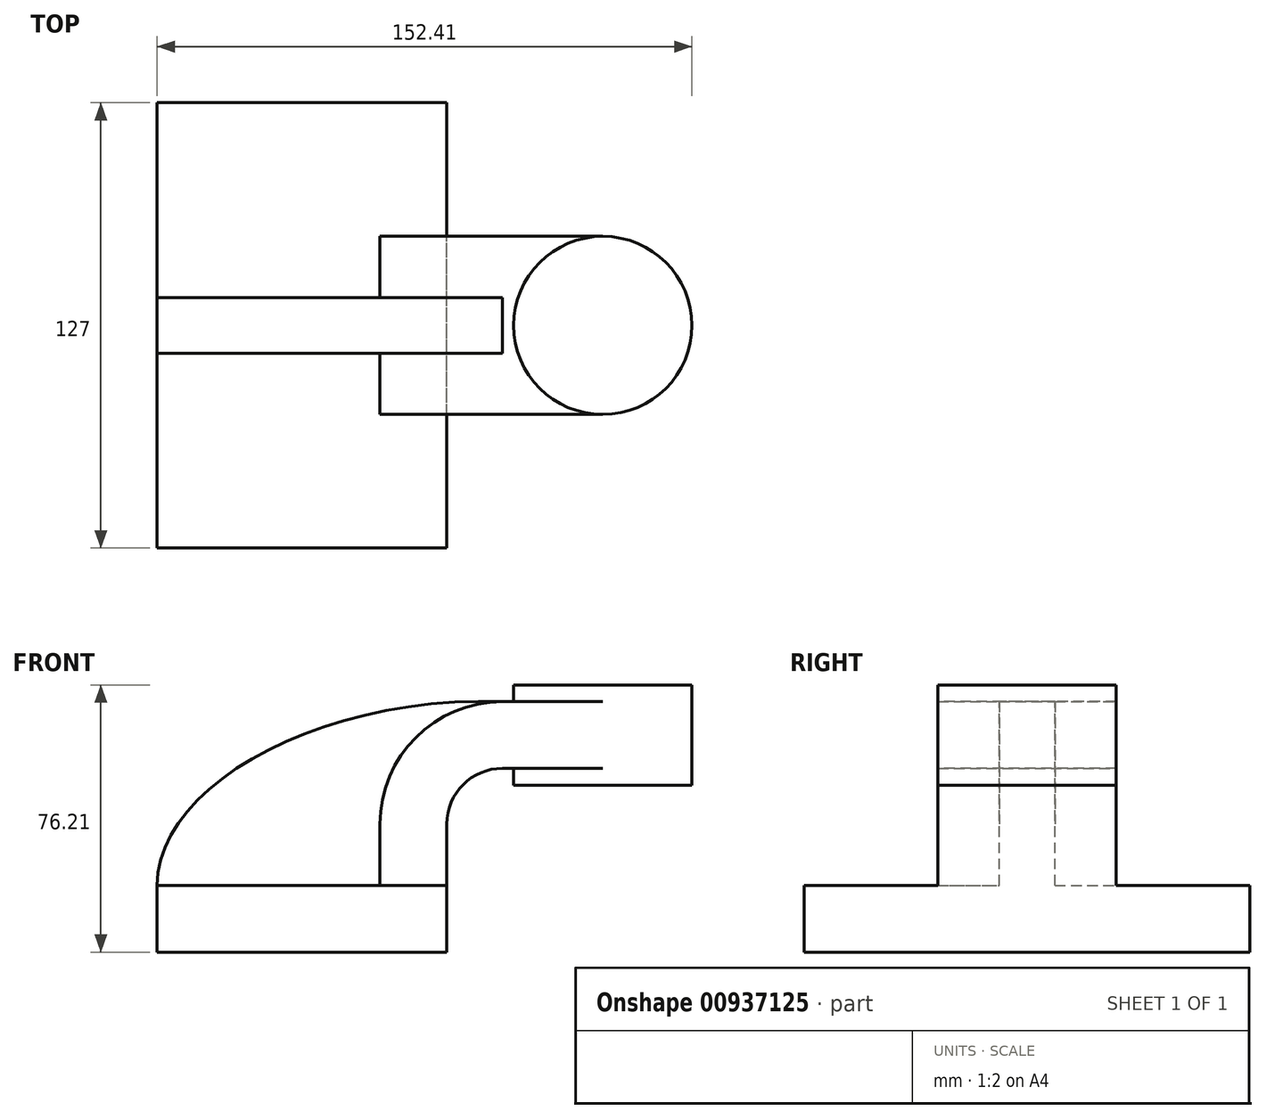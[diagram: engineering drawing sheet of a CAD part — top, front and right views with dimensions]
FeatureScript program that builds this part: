
annotation { "Feature Type Name" : "Feature", "Feature Type Description" : "" }
export const myFeature = defineFeature(function(context is Context, id is Id, definition is map)
    precondition{}
    {
        {
            var Q0;
            Q0=qCreatedBy(makeId("Front.planeOp"),FACE);
            var sketch = newSketch(context, id + "F0", { "sketchPlane" : qUnion([Q0])});
            skLineSegment(sketch, "E0.bottom", {"start": v(41.28, -9.52) * mm, "end": v(-41.28, -9.53) * mm});
            skLineSegment(sketch, "E0.top", {"start": v(41.28, 9.53) * mm, "end": v(-41.28, 9.53) * mm});
            skLineSegment(sketch, "E0.left", {"start": v(41.28, -9.52) * mm, "end": v(41.28, 9.53) * mm});
            skLineSegment(sketch, "E0.right", {"start": v(-41.28, -9.53) * mm, "end": v(-41.28, 9.53) * mm});
            skPoint(sketch, "E0.middle", {"position": v(0, 0) * mm});
            skLineSegment(sketch, "E1.bottom", {"start": v(60.32, 66.68) * mm, "end": v(111.12, 66.68) * mm});
            skLineSegment(sketch, "E1.top", {"start": v(60.32, 38.1) * mm, "end": v(111.12, 38.1) * mm});
            skLineSegment(sketch, "E1.left", {"start": v(60.32, 66.68) * mm, "end": v(60.32, 38.1) * mm});
            skLineSegment(sketch, "E1.right", {"start": v(111.12, 66.68) * mm, "end": v(111.12, 38.1) * mm});
            skPoint(sketch, "E1.middle", {"position": v(85.72, 52.39) * mm});
            skLineSegment(sketch, "E2", {"start": v(41.28, 9.53) * mm, "end": v(41.28, 27) * mm});
            skLineSegment(sketch, "E3", {"start": v(57.15, 42.88) * mm, "end": v(85.72, 42.88) * mm});
            skArc(sketch, "E4", {"start": v(57.15, 42.88) * mm, "mid": v(45.92, 38.23) * mm, "end": v(41.28, 27) * mm});
            skLineSegment(sketch, "E5", {"start": v(41.28, 9.53) * mm, "end": v(22.23, 9.53) * mm});
            skLineSegment(sketch, "E6", {"start": v(22.23, 9.53) * mm, "end": v(22.23, 27) * mm});
            skLineSegment(sketch, "E7.MirrorCS", {"start": v(57.15, 61.9) * mm, "end": v(85.72, 61.9) * mm});
            skArc(sketch, "E8", {"start": v(57.15, 61.9) * mm, "mid": v(32.46, 51.68) * mm, "end": v(22.23, 27) * mm});
            skFitSpline(sketch, "E9", {"points": [v(-41.28, 9.53) * mm, v(57.15, 61.9) * mm], "startDerivative": vector(0.12, 83.94) * mm, "endDerivative": vector(159.38, -5.32) * mm});
            skLineSegment(sketch, "E10", {"start": v(85.72, 66.68) * mm, "end": v(85.72, 38.1) * mm});
            skSolve(sketch);
        }
        {
            var Q0;
            Q0=makeQuery(id+"F0.imprint","IMPRINT",FACE,{"disambiguationData":[TD([[makeQuery(id+"F0.imprint","IMPRINT",EDGE,{"derivedFrom":sQuery(id+"F0.wireOp",EDGE,"E0.bottom")}),-1.0]])]});
            extrude(context, id + "F1", {"entities" : qUnion([Q0]), "endBound" : BoundingType.SYMMETRIC, "depth" : 127 * mm, "offsetDistance" : 25.4 * mm});
        }
        {
            var Q0;
            Q0=makeQuery(id+"F0.imprint","IMPRINT",FACE,{"disambiguationData":[TD([[makeQuery(id+"F0.imprint","IMPRINT",EDGE,{"derivedFrom":sQuery(id+"F0.wireOp",EDGE,"E2")}),1.0]])]});
            var Q1;
            {var subQ5=sQuery(id+"F0.wireOp",EDGE,"w8TjEk6U-2pLm-mTnR-tbfv-UJByZVcYHBu7");Q1=makeQuery(id+"F0.imprint","IMPRINT",FACE,{"disambiguationData":[TD([[makeQuery(id+"F0.imprint","IMPRINT",EDGE,{"derivedFrom":subQ5}),1.0]])]});}
            var Q2;
            {var subQ0=sQuery(id+"F0.wireOp",EDGE,"E7.MirrorCS");var subQ1=sQuery(id+"F0.wireOp",EDGE,"E1.left");var subQ2=makeQuery(id+"F0.imprint","INTERSECT",VERTEX,{"derivedFrom":[subQ1,subQ0]});Q2=makeQuery(id+"F0.imprint","IMPRINT",FACE,{"disambiguationData":[TD([[makeQuery(id+"F0.imprint","IMPRINT",EDGE,{"disambiguationData":[TD([[subQ2,-1.0]])],"derivedFrom":subQ1}),1.0]])]});}
            extrude(context, id + "F2", {"entities" : qUnion([Q0, Q1, Q2]), "operationType" : NewBodyOperationType.ADD, "endBound" : BoundingType.SYMMETRIC, "depth" : 50.8 * mm, "offsetDistance" : 25.4 * mm});
        }
        {
            var Q0;
            {var subQ0=sQuery(id+"F0.wireOp",EDGE,"E1.right");Q0=makeQuery(id+"F0.imprint","IMPRINT",FACE,{"disambiguationData":[TD([[makeQuery(id+"F0.imprint","IMPRINT",EDGE,{"derivedFrom":subQ0}),-1.0]])]});}
            var Q1;
            Q1=sQuery(id+"F0.wireOp",EDGE,"E10");
            revolve(context, id + "F3", {"operationType" : NewBodyOperationType.ADD, "surfaceOperationType" : NewSurfaceOperationType.NEW, "entities" : qUnion([Q0]), "axis" : qUnion([Q1]), "revolveType" : RevolveType.FULL});
        }
        {
            var Q0;
            Q0=makeQuery(id+"F0.imprint","IMPRINT",FACE,{"disambiguationData":[TD([[makeQuery(id+"F0.imprint","IMPRINT",EDGE,{"derivedFrom":sQuery(id+"F0.wireOp",EDGE,"E0.top")}),-1.0]])]});
            extrude(context, id + "F4", {"entities" : qUnion([Q0]), "operationType" : NewBodyOperationType.ADD, "endBound" : BoundingType.SYMMETRIC, "depth" : 15.88 * mm, "offsetDistance" : 25.4 * mm});
        }
    });
